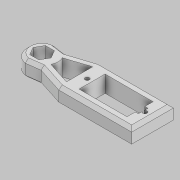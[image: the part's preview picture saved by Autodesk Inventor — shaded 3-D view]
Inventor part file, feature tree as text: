
AUTODESK INVENTOR PART (.ipt)
format: ipt  version: 2022.2 (Build 262287010, 287A)  size: 175,104 bytes
history: native  units: mm
features: extrude x3, sketch x3, chamfer x2, other x1, fillet x1
ambient origin geometry x8: Origin, YZ Plane, XZ Plane, XY Plane, X Axis, Y Axis, Z Axis, Center Point
bodies: Body1 (feature_tree)
feature tree (10):
  other  "Sólido1"
  extrude  "Extrusión1"  Depth=23.0mm
  extrude  "Extrusión2"  Depth=20.0mm
  extrude  "Extrusión3"  Depth=60.0mm
  chamfer  "Chaflán1"  Distance=7.5mm
  fillet  "Empalme1"  [1 undecoded]
  chamfer  "Chaflán2"  Distance=3.667mm
  sketch  "Boceto1"  dims[d1=35.0mm d2=23.0mm]
  sketch  "Boceto2"  dims[d3=12.5mm d4=20.0mm]
  sketch  "Boceto3"  dims[d6=14.0mm d7=60.0mm d8=7.5mm d9=0.0mm d10=3.667mm d11=0.0mm d13=8.0mm d14=0.0mm d15=6.0mm d16=6.0mm d17=30.0mm d18=30.0mm d19=2.0mm d20=2.0mm d21=27.7mm d22=0.0mm d23=0.0mm d24=4.6mm d25=0.0mm d26=0.0mm d27=1.5mm d28=2.0mm d29=45.0deg d30=6.0mm d31=1.5mm d32=2.0mm d33=45.0deg d34=1.5mm]
note: 1 required parameter value undecoded (feature->parameter linkage not recoverable at this tier; creation-order binding heuristic only, values carry confidence <= 0.55)
